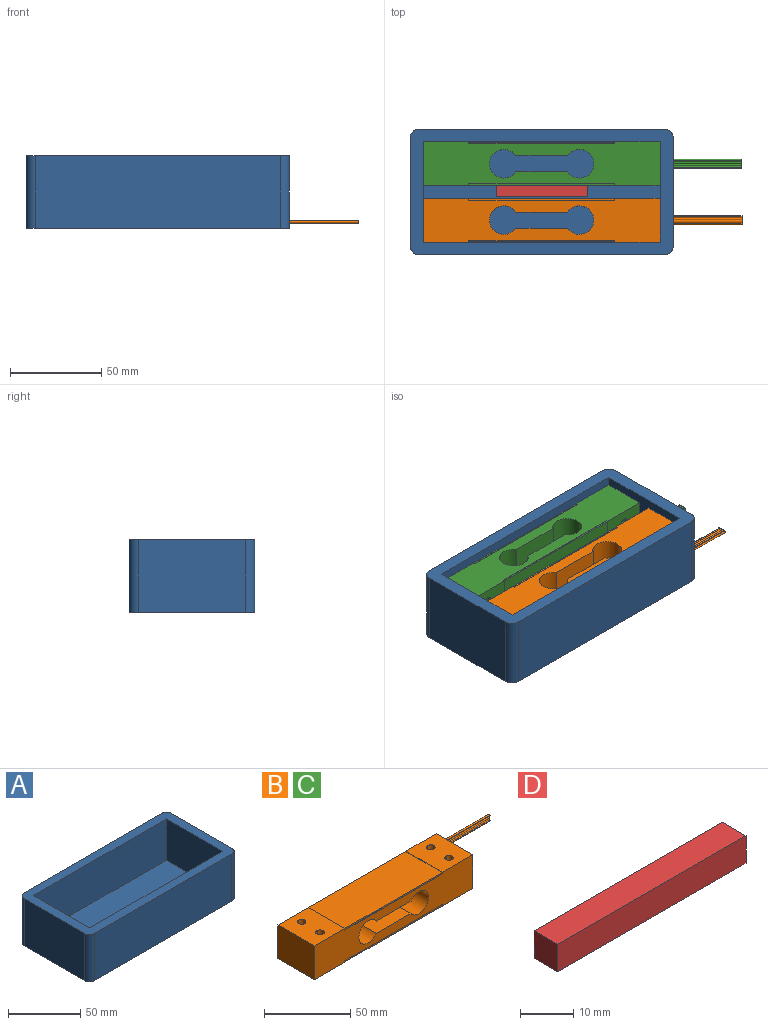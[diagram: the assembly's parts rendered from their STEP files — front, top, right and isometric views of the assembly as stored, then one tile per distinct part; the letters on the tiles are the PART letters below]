
ASSEMBLY  parts=4 mates=8
PART A: 15 faces, bbox 144.7x69x40 mm
  f0: plane 130x35mm, normal (0,1,0), area 4550mm2, adj f1,f7,f8,f10
  f1: plane 55x35mm, normal (1,0,0), area 1925mm2, adj f0,f2,f8,f10
  f2: plane 130x35mm, normal (0,-1,0), area 4550mm2, adj f1,f7,f8,f10
  f3: plane 59.01x40mm, normal (1,0,0), area 2360.5mm2, adj f8,f9,f11,f14
  f4: plane 134.67x40mm, normal (0,1,0), area 5386.8mm2, adj f8,f9,f11,f12
  f5: plane 59.01x40mm, normal (-1,0,0), area 2360.5mm2, adj f8,f9,f12,f13
  f6: plane 134.67x40mm, normal (0,-1,0), area 5386.8mm2, adj f8,f9,f13,f14
  f7: plane 55x35mm, normal (-1,0,0), area 1925mm2, adj f0,f2,f8,f10
  f8: plane 144.67x69.01mm, normal (0,0,1), area 2812.4mm2, adj f0,f1,f2,f3,f4,f5,f6,f7
  f9: plane 144.67x69.01mm, normal (0,0,-1), area 9962.4mm2, adj f3,f4,f5,f6,f11,f12,f13,f14
  f10: plane 130x55mm, normal (0,0,1), area 7150mm2, adj f0,f1,f2,f7
  f11: cylinder r=5mm len=40mm, axis (0,0,1), area 314.2mm2, adj f3,f4,f8,f9
  f12: cylinder r=5mm len=40mm, axis (0,0,-1), area 314.2mm2, adj f4,f5,f8,f9
  f13: cylinder r=5mm len=40mm, axis (0,0,1), area 314.2mm2, adj f5,f6,f8,f9
  f14: cylinder r=5mm len=40mm, axis (0,0,-1), area 314.2mm2, adj f3,f6,f8,f9
PART B: 57 faces, bbox 175x32.3x24 mm
  f0: torus R=1.5mm, axis (0,0,1), area 5.8mm2, adj f1,f5,f47,f55
  f1: cylinder r=0.63mm len=48.5mm, axis (1,0,0), area 94.6mm2, adj f0,f2,f48,f54
  f2: plane 5x1.25mm, normal (1,0,0), area 4.9mm2, adj f1,f3,f48,f49,f51,f52,f53,f54
  f3: cylinder r=0.63mm len=48.5mm, axis (1,0,0), area 94.6mm2, adj f2,f4,f49,f51
  f4: torus R=1.5mm, axis (0,0,1), area 3.4mm2, adj f3,f5,f47,f50
  f5: plane 130x24mm, normal (0,1,0), area 2317.2mm2, adj f0,f4,f6,f8,f9,f10,f11,f12
  f6: cylinder r=7.85mm len=30mm, axis (0,-1,0), area 1199.4mm2, adj f5,f7,f9,f10
  f7: plane 130x24mm, normal (0,-1,0), area 2322.2mm2, adj f6,f8,f9,f10,f11,f16,f17,f18
  f8: cylinder r=7.85mm len=30mm, axis (0,-1,0), area 1199.4mm2, adj f5,f7,f9,f10
  f9: plane 30x28.5mm, normal (0,0,-1), area 854.9mm2, adj f5,f6,f7,f8
  f10: plane 30x28.5mm, normal (0,0,1), area 854.9mm2, adj f5,f6,f7,f8
  f11: plane 30x1.1mm, normal (1,0,0), area 30mm2, adj f5,f7,f12,f13,f14,f15,f16,f29
  f12: plane 80x0.1mm, normal (0,0,-1), area 8mm2, adj f5,f11,f13,f17
  f13: plane 80x1mm, normal (0,1,0), area 79.8mm2, adj f11,f12,f14,f17,f43,f44,f45,f46
  f14: plane 29.8x0.1mm, normal (0,0,-1), area 3mm2, adj f11,f13,f15,f46
  f15: plane 80x1mm, normal (0,-1,0), area 79.8mm2, adj f11,f14,f16,f17,f43,f44,f45,f46
  f16: plane 80x0.1mm, normal (0,0,-1), area 8mm2, adj f7,f11,f15,f17
  f17: plane 30x1.1mm, normal (-1,0,0), area 30mm2, adj f5,f7,f12,f13,f15,f16,f18,f43
  f18: plane 30x25mm, normal (0,0,-1), area 712mm2, adj f5,f7,f17,f19,f39,f40,f41,f42
  f19: plane 30x24mm, normal (1,0,0), area 720mm2, adj f5,f7,f18,f20
  f20: plane 30x25mm, normal (0,0,1), area 712mm2, adj f5,f7,f19,f21,f39,f40,f41,f42
  f21: plane 30x1.1mm, normal (-1,0,0), area 30mm2, adj f5,f7,f20,f22,f23,f24,f25,f34
  f22: plane 80x1mm, normal (0,1,0), area 79.8mm2, adj f21,f23,f26,f34,f35,f36,f37,f38
  f23: plane 29.8x0.1mm, normal (0,0,1), area 3mm2, adj f21,f22,f24,f38
  f24: plane 80x1mm, normal (0,-1,0), area 79.8mm2, adj f21,f23,f25,f26,f35,f36,f37,f38
  f25: plane 80x0.1mm, normal (0,0,1), area 8mm2, adj f7,f21,f24,f26
  f26: plane 30x1.1mm, normal (1,0,0), area 30mm2, adj f5,f7,f22,f24,f25,f27,f34,f35
  f27: plane 30x25mm, normal (0,0,1), area 712mm2, adj f5,f7,f26,f28,f30,f31,f32,f33
  f28: plane 30x24mm, normal (-1,0,0), area 720mm2, adj f5,f7,f27,f29
  f29: plane 30x25mm, normal (0,0,-1), area 712mm2, adj f5,f7,f11,f28,f30,f31,f32,f33
  f30: cylinder r=2.46mm len=24mm, axis (0,0,-1), area 185.4mm2, adj f27,f29,f31
  f31: cylinder r=2.46mm len=24mm, axis (0,0,-1), area 185.4mm2, adj f27,f29,f30
  f32: cylinder r=2.46mm len=24mm, axis (0,0,-1), area 185.4mm2, adj f27,f29,f33
  f33: cylinder r=2.46mm len=24mm, axis (0,0,-1), area 185.4mm2, adj f27,f29,f32
  f34: plane 80x0.1mm, normal (0,0,1), area 8mm2, adj f5,f21,f22,f26
  f35: plane 29.8x0.1mm, normal (0,0,1), area 3mm2, adj f22,f24,f26,f36
  f36: plane 29.8x0.9mm, normal (-1,0,0), area 26.8mm2, adj f22,f24,f35,f37
  f37: plane 79.8x29.8mm, normal (0,0,1), area 2378mm2, adj f22,f24,f36,f38
  f38: plane 29.8x0.9mm, normal (1,0,0), area 26.8mm2, adj f22,f23,f24,f37
  f39: cylinder r=2.46mm len=24mm, axis (0,0,-1), area 185.4mm2, adj f18,f20,f40
  f40: cylinder r=2.46mm len=24mm, axis (0,0,-1), area 185.4mm2, adj f18,f20,f39
  f41: cylinder r=2.46mm len=24mm, axis (0,0,-1), area 185.4mm2, adj f18,f20,f42
  f42: cylinder r=2.46mm len=24mm, axis (0,0,-1), area 185.4mm2, adj f18,f20,f41
  f43: plane 29.8x0.1mm, normal (0,0,-1), area 3mm2, adj f13,f15,f17,f44
  f44: plane 29.8x0.9mm, normal (1,0,0), area 26.8mm2, adj f13,f15,f43,f45
  f45: plane 79.8x29.8mm, normal (0,0,-1), area 2378mm2, adj f13,f15,f44,f46
  f46: plane 29.8x0.9mm, normal (-1,0,0), area 26.8mm2, adj f13,f14,f15,f45
  f47: torus R=1.5mm, axis (0,0,1), area 9.2mm2, adj f0,f4,f5,f48,f49
  f48: cylinder r=0.62mm len=48.5mm, axis (1,0,0), area 142.6mm2, adj f1,f2,f47,f49
  f49: cylinder r=0.62mm len=48.5mm, axis (1,0,0), area 47.3mm2, adj f2,f3,f47,f48
  f50: torus R=1.5mm, axis (0,0,1), area 3.4mm2, adj f4,f5,f51,f56
  f51: cylinder r=0.63mm len=48.5mm, axis (1,0,0), area 94.6mm2, adj f2,f3,f50,f52
  f52: cylinder r=0.62mm len=48.5mm, axis (1,0,0), area 47.3mm2, adj f2,f51,f53,f56
  f53: cylinder r=0.62mm len=48.5mm, axis (1,0,0), area 142.6mm2, adj f2,f52,f54,f56
  f54: cylinder r=0.63mm len=48.5mm, axis (1,0,0), area 94.6mm2, adj f1,f2,f53,f55
  f55: torus R=1.5mm, axis (0,0,1), area 5.8mm2, adj f0,f5,f54,f56
  f56: torus R=1.5mm, axis (0,0,1), area 9.2mm2, adj f5,f50,f52,f53,f55
PART C: same geometry as B
PART D: 6 faces, bbox 50x6.3x6.3 mm
  f0: plane 6.3x6.3mm, normal (-1,0,0), area 39.7mm2, adj f1,f3,f4,f5
  f1: plane 50x6.3mm, normal (0,-1,0), area 315mm2, adj f0,f2,f4,f5
  f2: plane 6.3x6.3mm, normal (1,0,0), area 39.7mm2, adj f1,f3,f4,f5
  f3: plane 50x6.3mm, normal (0,1,0), area 315mm2, adj f0,f2,f4,f5
  f4: plane 50x6.3mm, normal (0,0,1), area 315mm2, adj f0,f1,f2,f3
  f5: plane 50x6.3mm, normal (0,0,-1), area 315mm2, adj f0,f1,f2,f3
PLACE A rot(axis=(1,0,0),0deg) t=(143.66,71.56,90.25)mm
PLACE B rot(axis=(-1,0,0),90deg) t=(143.66,56.06,110.25)mm
PLACE C rot(axis=(-1,0,0),90deg) t=(143.66,87.06,110.25)mm
PLACE D rot(axis=(1,0,0),0deg) t=(143.66,72.01,107.1)mm
MATE planar A.f2 <-> C.f27  axis (0,-1,0) through (143.66,99.06,112.75)mm
MATE planar B.f29 <-> A.f0  axis (0,-1,0) through (91.19,44.06,110.25)mm
MATE parallel C.f27 <-> A.f2  axis (0,1,0) through (91.19,99.06,110.25)mm
MATE planar D.f3 <-> C.f45  axis (0,1,0) through (143.66,75.16,110.25)mm
MATE planar B.f28 <-> A.f1  axis (-1,0,0) through (78.66,56.06,110.25)mm
MATE planar B.f5 <-> A.f10  axis (0,0,-1) through (143.53,56.06,95.25)mm
MATE planar A.f1 <-> C.f28  axis (1,0,0) through (78.66,71.56,112.75)mm
MATE planar C.f5 <-> A.f10  axis (0,0,-1) through (143.53,87.06,95.25)mm
